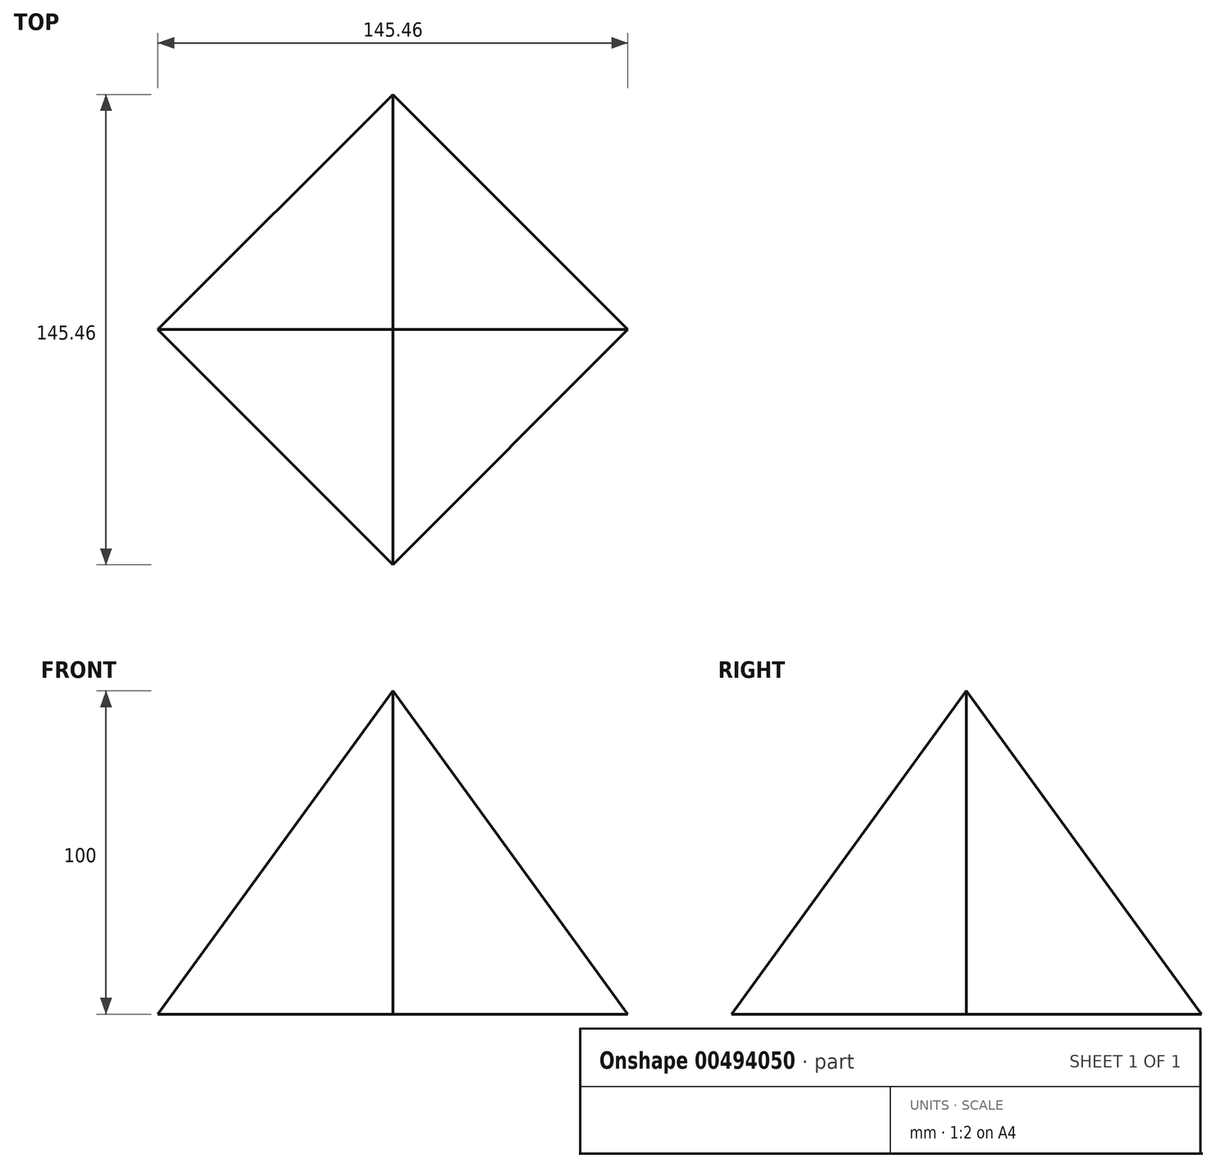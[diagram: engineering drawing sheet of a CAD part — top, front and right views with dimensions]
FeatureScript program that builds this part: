
annotation { "Feature Type Name" : "Feature", "Feature Type Description" : "" }
export const myFeature = defineFeature(function(context is Context, id is Id, definition is map)
    precondition{}
    {
        {
            var Q0;
            Q0=qCreatedBy(makeId("Top.planeOp"),FACE);
            var sketch = newSketch(context, id + "F0", { "sketchPlane" : qUnion([Q0])});
            skCircle(sketch, "E0.cCircle", {"center": v(0, 0) * mm, "radius": 72.73 * mm, "construction": true});
            skLineSegment(sketch, "E0.0", {"start": v(0, 72.73) * mm, "end": v(72.73, 0) * mm});
            skLineSegment(sketch, "E0.1", {"start": v(72.73, 0) * mm, "end": v(0, -72.73) * mm});
            skLineSegment(sketch, "E0.2", {"start": v(0, -72.73) * mm, "end": v(-72.73, 0) * mm});
            skLineSegment(sketch, "E0.3", {"start": v(-72.73, 0) * mm, "end": v(0, 72.73) * mm});
            skSolve(sketch);
        }
        {
            var Q0;
            Q0=qCreatedBy(makeId("Top.planeOp"),FACE);
            cPlane(context, id + "F1", {"entities" : qUnion([Q0]), "cplaneType" : CPlaneType.OFFSET, "offset" : 100 * mm, "width" : 150 * mm, "height" : 150 * mm});
        }
        {
            var Q0;
            Q0=qCreatedBy(id+"F1.planeOp",FACE);
            var sketch = newSketch(context, id + "F2", { "sketchPlane" : qUnion([Q0])});
            skPoint(sketch, "E1", {"position": v(0, 0) * mm});
            skSolve(sketch);
        }
        {
            var Q0;
            Q0=makeQuery(id+"F0.imprint","IMPRINT",FACE,{"disambiguationData":[TD([[makeQuery(id+"F0.imprint","IMPRINT",EDGE,{"derivedFrom":sQuery(id+"F0.wireOp",EDGE,"E0.0")}),-1.0]])]});
            var Q1;
            Q1=sQuery(id+"F2.wireOp",VERTEX,"E1");
            loft(context, id + "F3", {"sheetProfilesArray" : [{ "sheetProfileEntities" : qUnion([Q0]) }, { "sheetProfileEntities" : qUnion([Q1]) }]});
        }
    });
